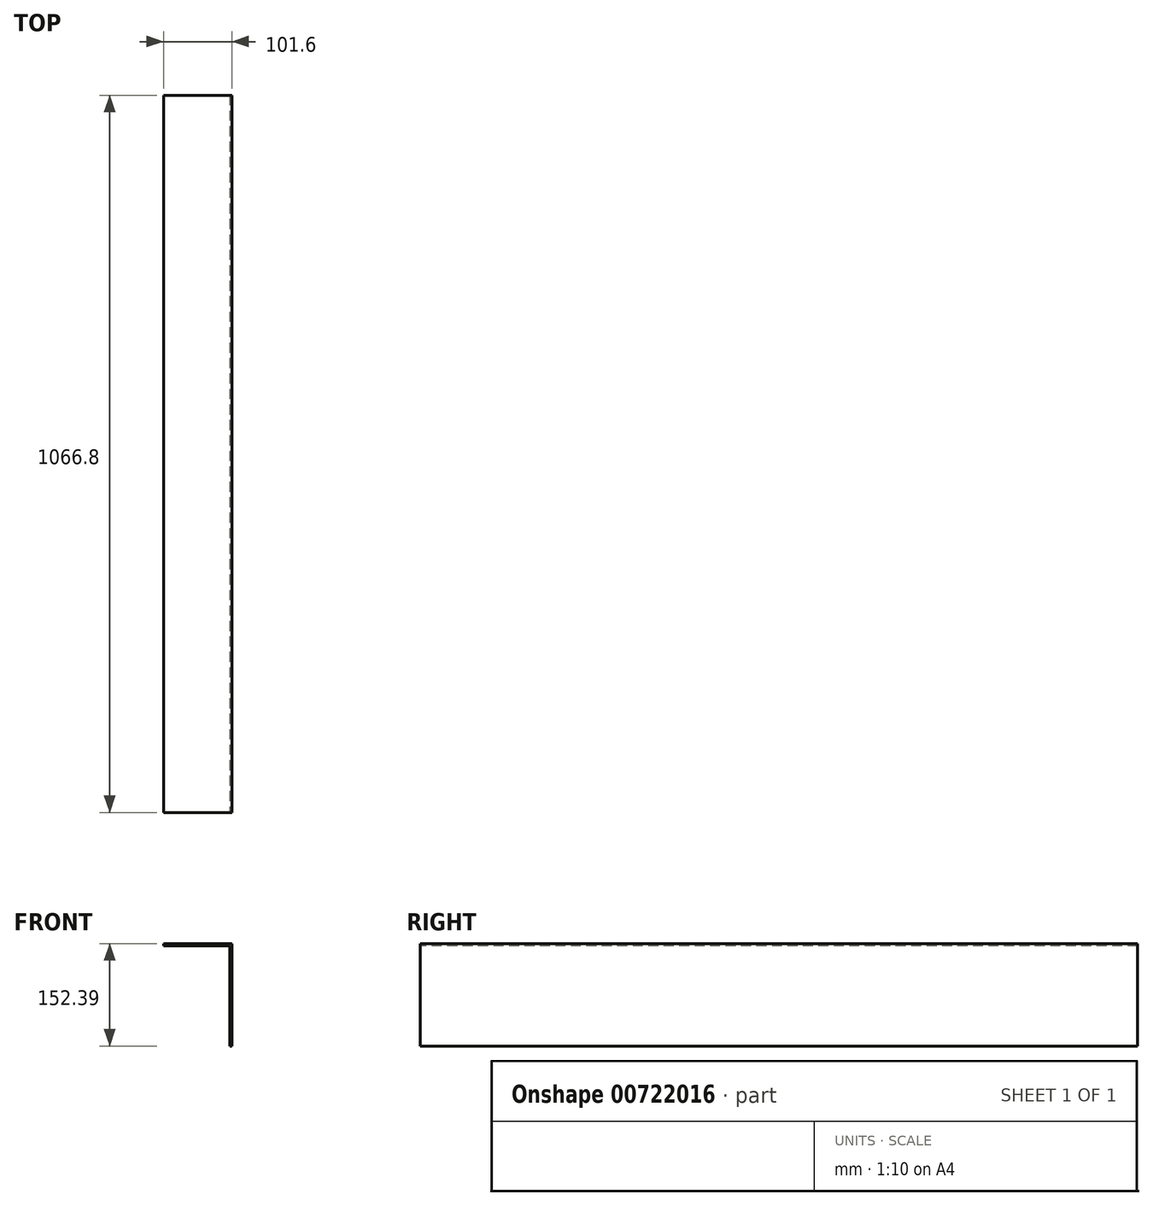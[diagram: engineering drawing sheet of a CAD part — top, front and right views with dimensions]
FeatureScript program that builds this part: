
annotation { "Feature Type Name" : "Feature", "Feature Type Description" : "" }
export const myFeature = defineFeature(function(context is Context, id is Id, definition is map)
    precondition{}
    {
        {
            var Q0;
            Q0=qCreatedBy(makeId("Top.planeOp"),FACE);
            var sketch = newSketch(context, id + "F0", { "sketchPlane" : qUnion([Q0])});
            skLineSegment(sketch, "E0.bottom", {"start": v(-79.2, 725.14) * mm, "end": v(22.4, 725.14) * mm});
            skLineSegment(sketch, "E0.top", {"start": v(-79.2, -341.66) * mm, "end": v(22.4, -341.66) * mm});
            skLineSegment(sketch, "E0.left", {"start": v(-79.2, 725.14) * mm, "end": v(-79.2, -341.66) * mm});
            skLineSegment(sketch, "E0.right", {"start": v(22.4, 725.14) * mm, "end": v(22.4, -341.66) * mm});
            skSolve(sketch);
        }
        {
            var Q0;
            Q0 = qSketchRegion(id + "F0", true);
            extrude(context, id + "F1", {"entities" : qUnion([Q0]), "depth" : 3.17 * mm, "offsetDistance" : 25.4 * mm});
        }
        {
            var Q0;
            Q0=makeQuery(id+"F1.opExtrude","CAP_FACE",FACE,{"disambiguationData":[OSD([sQuery(id+"F0.wireOp",EDGE,"E0.bottom"),sQuery(id+"F0.wireOp",EDGE,"E0.top"),sQuery(id+"F0.wireOp",EDGE,"E0.left"),sQuery(id+"F0.wireOp",EDGE,"E0.right")])],"isStart":false});
            var sketch = newSketch(context, id + "F2", { "sketchPlane" : qUnion([Q0])});
            skLineSegment(sketch, "E1.bottom", {"start": v(19.22, 725.14) * mm, "end": v(22.4, 725.14) * mm});
            skLineSegment(sketch, "E1.top", {"start": v(19.22, -341.66) * mm, "end": v(22.4, -341.66) * mm});
            skLineSegment(sketch, "E1.left", {"start": v(19.22, 725.14) * mm, "end": v(19.22, -341.66) * mm});
            skLineSegment(sketch, "E1.right", {"start": v(22.4, 725.14) * mm, "end": v(22.4, -341.66) * mm});
            skSolve(sketch);
        }
        {
            var Q0;
            Q0 = qSketchRegion(id + "F2", true);
            extrude(context, id + "F3", {"entities" : qUnion([Q0]), "operationType" : NewBodyOperationType.ADD, "oppositeDirection" : true, "depth" : 152.4 * mm, "offsetDistance" : 25.4 * mm});
        }
    });
